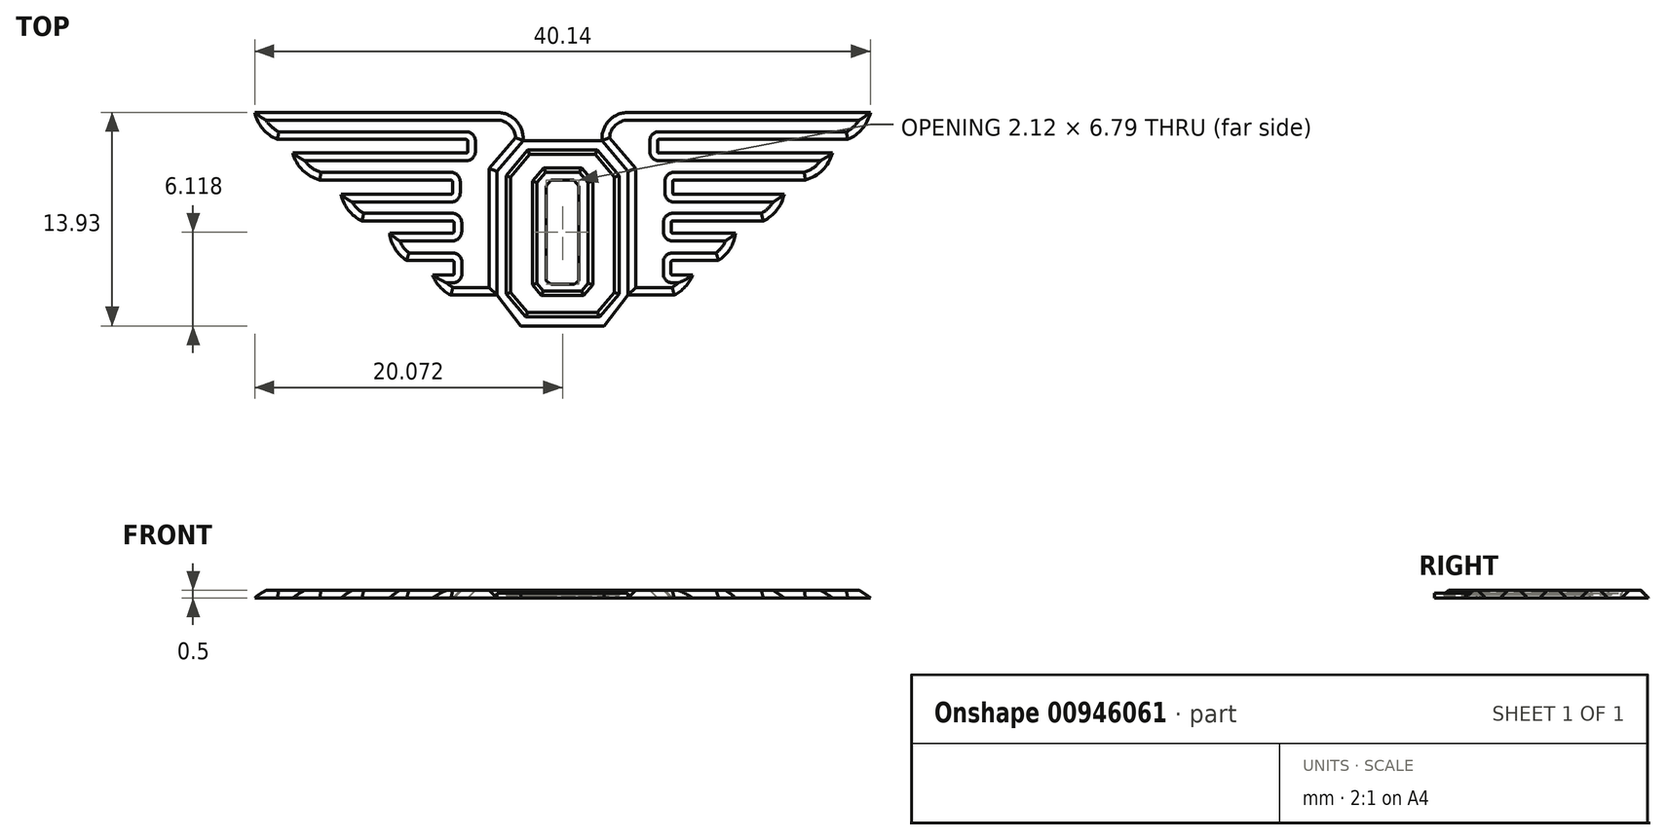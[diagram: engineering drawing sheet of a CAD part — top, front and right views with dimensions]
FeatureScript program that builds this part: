
annotation { "Feature Type Name" : "Feature", "Feature Type Description" : "" }
export const myFeature = defineFeature(function(context is Context, id is Id, definition is map)
    precondition{}
    {
        {
            var Q0;
            Q0=qCreatedBy(makeId("Top.planeOp"),FACE);
            var sketch = newSketch(context, id + "F0", { "sketchPlane" : qUnion([Q0])});
            skLineSegment(sketch, "E0", {"start": v(17.8, 9.2) * mm, "end": v(2, 9.2) * mm});
            skArc(sketch, "E1", {"start": v(2, 9.2) * mm, "mid": v(0.74, 8.65) * mm, "end": v(0.3, 7.37) * mm});
            skLineSegment(sketch, "E2", {"start": v(16.32, 7.44) * mm, "end": v(4, 7.44) * mm});
            skLineSegment(sketch, "E3", {"start": v(3.9, 7.34) * mm, "end": v(3.9, 6.65) * mm});
            skLineSegment(sketch, "E4", {"start": v(4, 6.55) * mm, "end": v(15.3, 6.55) * mm});
            skArc(sketch, "E5", {"start": v(16.32, 7.44) * mm, "mid": v(17.27, 8.14) * mm, "end": v(17.8, 9.2) * mm});
            skLineSegment(sketch, "E6", {"start": v(13.55, 4.8) * mm, "end": v(5, 4.8) * mm});
            skLineSegment(sketch, "E7", {"start": v(4.9, 4.7) * mm, "end": v(4.9, 3.95) * mm});
            skLineSegment(sketch, "E8", {"start": v(5, 3.85) * mm, "end": v(12.16, 3.85) * mm});
            skArc(sketch, "E9", {"start": v(13.55, 4.8) * mm, "mid": v(14.66, 5.44) * mm, "end": v(15.3, 6.55) * mm});
            skLineSegment(sketch, "E10", {"start": v(10.8, 2.12) * mm, "end": v(4.9, 2.12) * mm});
            skLineSegment(sketch, "E11", {"start": v(4.8, 2.02) * mm, "end": v(4.8, 1.42) * mm});
            skLineSegment(sketch, "E12", {"start": v(4.9, 1.32) * mm, "end": v(9, 1.32) * mm});
            skArc(sketch, "E13", {"start": v(10.8, 2.12) * mm, "mid": v(11.68, 2.83) * mm, "end": v(12.16, 3.85) * mm});
            skLineSegment(sketch, "E14", {"start": v(7.89, -0.47) * mm, "end": v(4.89, -0.47) * mm});
            skLineSegment(sketch, "E15", {"start": v(4.79, -0.57) * mm, "end": v(4.79, -1.32) * mm});
            skLineSegment(sketch, "E16", {"start": v(4.89, -1.42) * mm, "end": v(6.2, -1.42) * mm});
            skArc(sketch, "E17", {"start": v(7.89, -0.47) * mm, "mid": v(8.64, 0.3) * mm, "end": v(9, 1.32) * mm});
            skLineSegment(sketch, "E18", {"start": v(5, -2.71) * mm, "end": v(2, -2.71) * mm});
            skLineSegment(sketch, "E19", {"start": v(-2.28, -2) * mm, "end": v(-1.52, -2) * mm});
            skLineSegment(sketch, "E20", {"start": v(-1.52, -2) * mm, "end": v(-1.22, -1.78) * mm});
            skLineSegment(sketch, "E21", {"start": v(-1.22, -1.78) * mm, "end": v(-1.22, 4.4) * mm});
            skLineSegment(sketch, "E22", {"start": v(-1.22, 4.4) * mm, "end": v(-1.53, 4.78) * mm});
            skLineSegment(sketch, "E23", {"start": v(-1.53, 4.78) * mm, "end": v(-2.28, 4.78) * mm});
            skLineSegment(sketch, "E24", {"start": v(-2.28, -5.31) * mm, "end": v(-2.28, 10.14) * mm, "construction": true});
            skArc(sketch, "E25", {"start": v(5, -2.71) * mm, "mid": v(5.71, -2.17) * mm, "end": v(6.2, -1.42) * mm});
            skLineSegment(sketch, "E26", {"start": v(2, -2.71) * mm, "end": v(2, 5.35) * mm});
            skLineSegment(sketch, "E27", {"start": v(2, 5.35) * mm, "end": v(0.3, 7.37) * mm});
            skLineSegment(sketch, "E28", {"start": v(2, -2.71) * mm, "end": v(0.44, -4.73) * mm});
            skLineSegment(sketch, "E29", {"start": v(0.44, -4.73) * mm, "end": v(-2.28, -4.73) * mm});
            skLineSegment(sketch, "E30", {"start": v(0.3, 7.37) * mm, "end": v(-2.28, 7.37) * mm});
            skLineSegment(sketch, "E31", {"start": v(1.4, -2.65) * mm, "end": v(1.4, 4.29) * mm});
            skLineSegment(sketch, "E32", {"start": v(1.4, -2.65) * mm, "end": v(0.13, -4.13) * mm});
            skLineSegment(sketch, "E33", {"start": v(0.13, -4.13) * mm, "end": v(-2.28, -4.13) * mm});
            skLineSegment(sketch, "E34", {"start": v(1.4, 4.29) * mm, "end": v(1.4, 5.08) * mm});
            skLineSegment(sketch, "E35", {"start": v(1.4, 5.08) * mm, "end": v(0, 6.77) * mm});
            skLineSegment(sketch, "E36", {"start": v(0, 6.77) * mm, "end": v(-2.28, 6.77) * mm});
            skLineSegment(sketch, "E37.MirrorCS", {"start": v(-4.85, 7.37) * mm, "end": v(-2.28, 7.37) * mm});
            skLineSegment(sketch, "E38.MirrorCS", {"start": v(-4.56, 6.77) * mm, "end": v(-2.28, 6.77) * mm});
            skLineSegment(sketch, "E39.MirrorCS", {"start": v(-6.55, 5.35) * mm, "end": v(-4.85, 7.37) * mm});
            skLineSegment(sketch, "E40.MirrorCS", {"start": v(-5.95, 5.08) * mm, "end": v(-4.56, 6.77) * mm});
            skLineSegment(sketch, "E41.MirrorCS", {"start": v(-5.95, -2.65) * mm, "end": v(-5.95, 4.29) * mm});
            skLineSegment(sketch, "E42.MirrorCS", {"start": v(-5.95, 4.29) * mm, "end": v(-5.95, 5.08) * mm});
            skLineSegment(sketch, "E43.MirrorCS", {"start": v(-6.55, -2.71) * mm, "end": v(-6.55, 5.35) * mm});
            skLineSegment(sketch, "E44.MirrorCS", {"start": v(-5.95, -2.65) * mm, "end": v(-4.69, -4.13) * mm});
            skLineSegment(sketch, "E45.MirrorCS", {"start": v(-6.55, -2.71) * mm, "end": v(-5, -4.73) * mm});
            skLineSegment(sketch, "E46.MirrorCS", {"start": v(-5, -4.73) * mm, "end": v(-2.28, -4.73) * mm});
            skLineSegment(sketch, "E47.MirrorCS", {"start": v(-4.69, -4.13) * mm, "end": v(-2.28, -4.13) * mm});
            skLineSegment(sketch, "E48.MirrorCS", {"start": v(-2.28, -2) * mm, "end": v(-3.03, -2) * mm});
            skLineSegment(sketch, "E49.MirrorCS", {"start": v(-3.03, -2) * mm, "end": v(-3.34, -1.78) * mm});
            skLineSegment(sketch, "E50.MirrorCS", {"start": v(-3.34, -1.78) * mm, "end": v(-3.34, 4.4) * mm});
            skLineSegment(sketch, "E51.MirrorCS", {"start": v(-3.34, 4.4) * mm, "end": v(-3.02, 4.78) * mm});
            skLineSegment(sketch, "E52.MirrorCS", {"start": v(-3.02, 4.78) * mm, "end": v(-2.28, 4.78) * mm});
            skLineSegment(sketch, "E53.MirrorCS", {"start": v(-9.55, -2.71) * mm, "end": v(-6.55, -2.71) * mm});
            skArc(sketch, "E54.MirrorCS", {"start": v(-9.55, -2.71) * mm, "mid": v(-10.27, -2.17) * mm, "end": v(-10.75, -1.42) * mm});
            skLineSegment(sketch, "E55.MirrorCS", {"start": v(-9.44, -1.42) * mm, "end": v(-10.75, -1.42) * mm});
            skLineSegment(sketch, "E56.MirrorCS", {"start": v(-9.34, -0.57) * mm, "end": v(-9.34, -1.32) * mm});
            skLineSegment(sketch, "E57.MirrorCS", {"start": v(-12.44, -0.47) * mm, "end": v(-9.44, -0.47) * mm});
            skArc(sketch, "E58.MirrorCS", {"start": v(-12.44, -0.47) * mm, "mid": v(-13.2, 0.3) * mm, "end": v(-13.56, 1.32) * mm});
            skLineSegment(sketch, "E59.MirrorCS", {"start": v(-9.46, 1.32) * mm, "end": v(-13.56, 1.32) * mm});
            skLineSegment(sketch, "E60.MirrorCS", {"start": v(-9.36, 2.02) * mm, "end": v(-9.36, 1.42) * mm});
            skLineSegment(sketch, "E61.MirrorCS", {"start": v(-15.36, 2.12) * mm, "end": v(-9.46, 2.12) * mm});
            skArc(sketch, "E62.MirrorCS", {"start": v(-15.36, 2.12) * mm, "mid": v(-16.24, 2.83) * mm, "end": v(-16.72, 3.85) * mm});
            skLineSegment(sketch, "E63.MirrorCS", {"start": v(-9.55, 3.85) * mm, "end": v(-16.72, 3.85) * mm});
            skLineSegment(sketch, "E64.MirrorCS", {"start": v(-9.45, 4.7) * mm, "end": v(-9.45, 3.95) * mm});
            skLineSegment(sketch, "E65.MirrorCS", {"start": v(-18.1, 4.8) * mm, "end": v(-9.55, 4.8) * mm});
            skArc(sketch, "E66.MirrorCS", {"start": v(-18.1, 4.8) * mm, "mid": v(-19.22, 5.44) * mm, "end": v(-19.86, 6.55) * mm});
            skLineSegment(sketch, "E67.MirrorCS", {"start": v(-8.56, 6.55) * mm, "end": v(-19.86, 6.55) * mm});
            skLineSegment(sketch, "E68.MirrorCS", {"start": v(-8.46, 7.34) * mm, "end": v(-8.46, 6.65) * mm});
            skLineSegment(sketch, "E69.MirrorCS", {"start": v(-20.87, 7.44) * mm, "end": v(-8.56, 7.44) * mm});
            skArc(sketch, "E70.MirrorCS", {"start": v(-20.87, 7.44) * mm, "mid": v(-21.82, 8.14) * mm, "end": v(-22.35, 9.2) * mm});
            skLineSegment(sketch, "E71.MirrorCS", {"start": v(-22.35, 9.2) * mm, "end": v(-6.55, 9.2) * mm});
            skArc(sketch, "E72.MirrorCS", {"start": v(-6.55, 9.2) * mm, "mid": v(-5.3, 8.65) * mm, "end": v(-4.85, 7.37) * mm});
            skPoint(sketch, "E73.visualSharp", {"position": v(-9.36, 1.32) * mm});
            skArc(sketch, "E73.filletArc", {"start": v(-9.46, 1.32) * mm, "mid": v(-9.38, 1.35) * mm, "end": v(-9.36, 1.42) * mm});
            skPoint(sketch, "E74.visualSharp", {"position": v(-9.36, 2.12) * mm});
            skArc(sketch, "E74.filletArc", {"start": v(-9.36, 2.02) * mm, "mid": v(-9.38, 2.09) * mm, "end": v(-9.46, 2.12) * mm});
            skPoint(sketch, "E75.visualSharp", {"position": v(-9.34, -0.47) * mm});
            skArc(sketch, "E75.filletArc", {"start": v(-9.34, -0.57) * mm, "mid": v(-9.37, -0.5) * mm, "end": v(-9.44, -0.47) * mm});
            skPoint(sketch, "E76.visualSharp", {"position": v(-9.34, -1.42) * mm});
            skArc(sketch, "E76.filletArc", {"start": v(-9.44, -1.42) * mm, "mid": v(-9.37, -1.39) * mm, "end": v(-9.34, -1.32) * mm});
            skPoint(sketch, "E77.visualSharp", {"position": v(-9.45, 3.85) * mm});
            skArc(sketch, "E77.filletArc", {"start": v(-9.55, 3.85) * mm, "mid": v(-9.48, 3.88) * mm, "end": v(-9.45, 3.95) * mm});
            skPoint(sketch, "E78.visualSharp", {"position": v(-9.45, 4.8) * mm});
            skArc(sketch, "E78.filletArc", {"start": v(-9.45, 4.7) * mm, "mid": v(-9.48, 4.76) * mm, "end": v(-9.55, 4.8) * mm});
            skPoint(sketch, "E79.visualSharp", {"position": v(-8.46, 6.55) * mm});
            skArc(sketch, "E79.filletArc", {"start": v(-8.56, 6.55) * mm, "mid": v(-8.5, 6.58) * mm, "end": v(-8.46, 6.65) * mm});
            skPoint(sketch, "E80.visualSharp", {"position": v(-8.46, 7.44) * mm});
            skArc(sketch, "E80.filletArc", {"start": v(-8.46, 7.34) * mm, "mid": v(-8.5, 7.41) * mm, "end": v(-8.56, 7.44) * mm});
            skPoint(sketch, "E81.visualSharp", {"position": v(3.9, 7.44) * mm});
            skArc(sketch, "E81.filletArc", {"start": v(4, 7.44) * mm, "mid": v(3.94, 7.41) * mm, "end": v(3.9, 7.34) * mm});
            skPoint(sketch, "E82.visualSharp", {"position": v(3.9, 6.55) * mm});
            skArc(sketch, "E82.filletArc", {"start": v(3.9, 6.65) * mm, "mid": v(3.94, 6.58) * mm, "end": v(4, 6.55) * mm});
            skPoint(sketch, "E83.visualSharp", {"position": v(4.9, 4.8) * mm});
            skArc(sketch, "E83.filletArc", {"start": v(5, 4.8) * mm, "mid": v(4.93, 4.76) * mm, "end": v(4.9, 4.7) * mm});
            skPoint(sketch, "E84.visualSharp", {"position": v(4.9, 3.85) * mm});
            skArc(sketch, "E84.filletArc", {"start": v(4.9, 3.95) * mm, "mid": v(4.93, 3.88) * mm, "end": v(5, 3.85) * mm});
            skPoint(sketch, "E85.visualSharp", {"position": v(4.8, 2.12) * mm});
            skArc(sketch, "E85.filletArc", {"start": v(4.9, 2.12) * mm, "mid": v(4.83, 2.09) * mm, "end": v(4.8, 2.02) * mm});
            skPoint(sketch, "E86.visualSharp", {"position": v(4.8, 1.32) * mm});
            skArc(sketch, "E86.filletArc", {"start": v(4.8, 1.42) * mm, "mid": v(4.83, 1.35) * mm, "end": v(4.9, 1.32) * mm});
            skPoint(sketch, "E87.visualSharp", {"position": v(4.79, -0.47) * mm});
            skArc(sketch, "E87.filletArc", {"start": v(4.89, -0.47) * mm, "mid": v(4.82, -0.5) * mm, "end": v(4.79, -0.57) * mm});
            skPoint(sketch, "E88.visualSharp", {"position": v(4.79, -1.42) * mm});
            skArc(sketch, "E88.filletArc", {"start": v(4.79, -1.32) * mm, "mid": v(4.82, -1.39) * mm, "end": v(4.89, -1.42) * mm});
            skLineSegment(sketch, "E89", {"start": v(-2.28, 5.29) * mm, "end": v(-1.18, 5.29) * mm});
            skLineSegment(sketch, "E90", {"start": v(-1.18, 5.29) * mm, "end": v(-0.6, 4.62) * mm});
            skLineSegment(sketch, "E91", {"start": v(-0.6, 4.62) * mm, "end": v(-0.6, -1.94) * mm});
            skLineSegment(sketch, "E92", {"start": v(-0.6, -1.94) * mm, "end": v(-1.03, -2.44) * mm});
            skLineSegment(sketch, "E93", {"start": v(-1.03, -2.44) * mm, "end": v(-2.28, -2.44) * mm});
            skLineSegment(sketch, "E94.MirrorCS", {"start": v(-2.28, 5.29) * mm, "end": v(-3.38, 5.29) * mm});
            skLineSegment(sketch, "E95.MirrorCS", {"start": v(-3.38, 5.29) * mm, "end": v(-3.95, 4.62) * mm});
            skLineSegment(sketch, "E96.MirrorCS", {"start": v(-3.95, 4.62) * mm, "end": v(-3.95, -1.94) * mm});
            skLineSegment(sketch, "E97.MirrorCS", {"start": v(-3.95, -1.94) * mm, "end": v(-3.53, -2.44) * mm});
            skLineSegment(sketch, "E98.MirrorCS", {"start": v(-3.53, -2.44) * mm, "end": v(-2.28, -2.44) * mm});
            skLineSegment(sketch, "E99", {"start": v(2, -2.91) * mm, "end": v(0.3, 7.37) * mm, "construction": true});
            skSolve(sketch);
        }
        {
            var Q0;
            Q0=makeQuery(id+"F0.imprint","IMPRINT",FACE,{"disambiguationData":[TD([[makeQuery(id+"F0.imprint","IMPRINT",EDGE,{"derivedFrom":sQuery(id+"F0.wireOp",EDGE,"E31")}),1.0]])]});
            var Q1;
            Q1=makeQuery(id+"F0.imprint","IMPRINT",FACE,{"disambiguationData":[TD([[makeQuery(id+"F0.imprint","IMPRINT",EDGE,{"derivedFrom":sQuery(id+"F0.wireOp",EDGE,"E0")}),1.0]])]});
            var Q2;
            Q2=makeQuery(id+"F0.imprint","IMPRINT",FACE,{"disambiguationData":[TD([[makeQuery(id+"F0.imprint","IMPRINT",EDGE,{"derivedFrom":sQuery(id+"F0.wireOp",EDGE,"E39.MirrorCS")}),1.0]])]});
            extrude(context, id + "F1", {"entities" : qUnion([Q0, Q1, Q2]), "depth" : 0.5 * mm, "offsetDistance" : 25 * mm});
        }
        {
            var Q0;
            Q0=makeQuery(id+"F0.imprint","IMPRINT",FACE,{"disambiguationData":[TD([[makeQuery(id+"F0.imprint","IMPRINT",EDGE,{"derivedFrom":sQuery(id+"F0.wireOp",EDGE,"E26")}),1.0]])]});
            var Q1;
            Q1=makeQuery(id+"F0.imprint","IMPRINT",FACE,{"disambiguationData":[TD([[makeQuery(id+"F0.imprint","IMPRINT",EDGE,{"derivedFrom":sQuery(id+"F0.wireOp",EDGE,"E19")}),-1.0]])]});
            extrude(context, id + "F2", {"entities" : qUnion([Q0, Q1]), "depth" : 0.3 * mm, "offsetDistance" : 25 * mm});
        }
        {
            var Q0;
            Q0=makeQuery(id+"F1.opExtrude","CAP_FACE",FACE,{"disambiguationData":[OSD([sQuery(id+"F0.wireOp",EDGE,"E39.MirrorCS"),sQuery(id+"F0.wireOp",EDGE,"E43.MirrorCS"),sQuery(id+"F0.wireOp",EDGE,"E53.MirrorCS"),sQuery(id+"F0.wireOp",EDGE,"E54.MirrorCS"),sQuery(id+"F0.wireOp",EDGE,"E55.MirrorCS"),sQuery(id+"F0.wireOp",EDGE,"E56.MirrorCS"),sQuery(id+"F0.wireOp",EDGE,"E57.MirrorCS"),sQuery(id+"F0.wireOp",EDGE,"E58.MirrorCS"),sQuery(id+"F0.wireOp",EDGE,"E59.MirrorCS"),sQuery(id+"F0.wireOp",EDGE,"E60.MirrorCS"),sQuery(id+"F0.wireOp",EDGE,"E61.MirrorCS"),sQuery(id+"F0.wireOp",EDGE,"E62.MirrorCS"),sQuery(id+"F0.wireOp",EDGE,"E63.MirrorCS"),sQuery(id+"F0.wireOp",EDGE,"E64.MirrorCS"),sQuery(id+"F0.wireOp",EDGE,"E65.MirrorCS"),sQuery(id+"F0.wireOp",EDGE,"E66.MirrorCS"),sQuery(id+"F0.wireOp",EDGE,"E67.MirrorCS"),sQuery(id+"F0.wireOp",EDGE,"E68.MirrorCS"),sQuery(id+"F0.wireOp",EDGE,"E69.MirrorCS"),sQuery(id+"F0.wireOp",EDGE,"E70.MirrorCS"),sQuery(id+"F0.wireOp",EDGE,"E71.MirrorCS"),sQuery(id+"F0.wireOp",EDGE,"E72.MirrorCS"),sQuery(id+"F0.wireOp",EDGE,"E73.filletArc"),sQuery(id+"F0.wireOp",EDGE,"E74.filletArc"),sQuery(id+"F0.wireOp",EDGE,"E75.filletArc"),sQuery(id+"F0.wireOp",EDGE,"E76.filletArc"),sQuery(id+"F0.wireOp",EDGE,"E77.filletArc"),sQuery(id+"F0.wireOp",EDGE,"E78.filletArc"),sQuery(id+"F0.wireOp",EDGE,"E79.filletArc"),sQuery(id+"F0.wireOp",EDGE,"E80.filletArc")])],"isStart":false});
            var Q1;
            Q1=makeQuery(id+"F1.opExtrude","CAP_FACE",FACE,{"disambiguationData":[OSD([sQuery(id+"F0.wireOp",EDGE,"E0"),sQuery(id+"F0.wireOp",EDGE,"E1"),sQuery(id+"F0.wireOp",EDGE,"E2"),sQuery(id+"F0.wireOp",EDGE,"E3"),sQuery(id+"F0.wireOp",EDGE,"E4"),sQuery(id+"F0.wireOp",EDGE,"E5"),sQuery(id+"F0.wireOp",EDGE,"E6"),sQuery(id+"F0.wireOp",EDGE,"E7"),sQuery(id+"F0.wireOp",EDGE,"E8"),sQuery(id+"F0.wireOp",EDGE,"E9"),sQuery(id+"F0.wireOp",EDGE,"E10"),sQuery(id+"F0.wireOp",EDGE,"E11"),sQuery(id+"F0.wireOp",EDGE,"E12"),sQuery(id+"F0.wireOp",EDGE,"E13"),sQuery(id+"F0.wireOp",EDGE,"E14"),sQuery(id+"F0.wireOp",EDGE,"E15"),sQuery(id+"F0.wireOp",EDGE,"E16"),sQuery(id+"F0.wireOp",EDGE,"E17"),sQuery(id+"F0.wireOp",EDGE,"E18"),sQuery(id+"F0.wireOp",EDGE,"E25"),sQuery(id+"F0.wireOp",EDGE,"E26"),sQuery(id+"F0.wireOp",EDGE,"E27"),sQuery(id+"F0.wireOp",EDGE,"E81.filletArc"),sQuery(id+"F0.wireOp",EDGE,"E82.filletArc"),sQuery(id+"F0.wireOp",EDGE,"E83.filletArc"),sQuery(id+"F0.wireOp",EDGE,"E84.filletArc"),sQuery(id+"F0.wireOp",EDGE,"E85.filletArc"),sQuery(id+"F0.wireOp",EDGE,"E86.filletArc"),sQuery(id+"F0.wireOp",EDGE,"E87.filletArc"),sQuery(id+"F0.wireOp",EDGE,"E88.filletArc")])],"isStart":false});
            chamfer(context, id + "F3", {"entities" : qUnion([Q0, Q1]), "width" : 0.5 * mm, "tangentPropagation" : true});
        }
        {
            var Q0;
            Q0=makeQuery(id+"F1.opExtrude","CAP_FACE",FACE,{"disambiguationData":[OSD([sQuery(id+"F0.wireOp",EDGE,"E31"),sQuery(id+"F0.wireOp",EDGE,"E32"),sQuery(id+"F0.wireOp",EDGE,"E33"),sQuery(id+"F0.wireOp",EDGE,"E34"),sQuery(id+"F0.wireOp",EDGE,"E35"),sQuery(id+"F0.wireOp",EDGE,"E36"),sQuery(id+"F0.wireOp",EDGE,"E38.MirrorCS"),sQuery(id+"F0.wireOp",EDGE,"E40.MirrorCS"),sQuery(id+"F0.wireOp",EDGE,"E41.MirrorCS"),sQuery(id+"F0.wireOp",EDGE,"E42.MirrorCS"),sQuery(id+"F0.wireOp",EDGE,"E44.MirrorCS"),sQuery(id+"F0.wireOp",EDGE,"E47.MirrorCS"),sQuery(id+"F0.wireOp",EDGE,"E89"),sQuery(id+"F0.wireOp",EDGE,"E90"),sQuery(id+"F0.wireOp",EDGE,"E91"),sQuery(id+"F0.wireOp",EDGE,"E92"),sQuery(id+"F0.wireOp",EDGE,"E93"),sQuery(id+"F0.wireOp",EDGE,"E94.MirrorCS"),sQuery(id+"F0.wireOp",EDGE,"E95.MirrorCS"),sQuery(id+"F0.wireOp",EDGE,"E96.MirrorCS"),sQuery(id+"F0.wireOp",EDGE,"E97.MirrorCS"),sQuery(id+"F0.wireOp",EDGE,"E98.MirrorCS")])],"isStart":false});
            chamfer(context, id + "F4", {"entities" : qUnion([Q0]), "width" : 0.3 * mm, "tangentPropagation" : true});
        }
        {
            var Q0;
            Q0=makeQuery(id+"F2.opExtrude","SWEPT_BODY",BODY,{"disambiguationData":[OSD([sQuery(id+"F0.wireOp",EDGE,"E26"),sQuery(id+"F0.wireOp",EDGE,"E27"),sQuery(id+"F0.wireOp",EDGE,"E28"),sQuery(id+"F0.wireOp",EDGE,"E29"),sQuery(id+"F0.wireOp",EDGE,"E30"),sQuery(id+"F0.wireOp",EDGE,"E31"),sQuery(id+"F0.wireOp",EDGE,"E32"),sQuery(id+"F0.wireOp",EDGE,"E33"),sQuery(id+"F0.wireOp",EDGE,"E34"),sQuery(id+"F0.wireOp",EDGE,"E35"),sQuery(id+"F0.wireOp",EDGE,"E36"),sQuery(id+"F0.wireOp",EDGE,"E37.MirrorCS"),sQuery(id+"F0.wireOp",EDGE,"E38.MirrorCS"),sQuery(id+"F0.wireOp",EDGE,"E39.MirrorCS"),sQuery(id+"F0.wireOp",EDGE,"E40.MirrorCS"),sQuery(id+"F0.wireOp",EDGE,"E41.MirrorCS"),sQuery(id+"F0.wireOp",EDGE,"E42.MirrorCS"),sQuery(id+"F0.wireOp",EDGE,"E43.MirrorCS"),sQuery(id+"F0.wireOp",EDGE,"E44.MirrorCS"),sQuery(id+"F0.wireOp",EDGE,"E45.MirrorCS"),sQuery(id+"F0.wireOp",EDGE,"E46.MirrorCS"),sQuery(id+"F0.wireOp",EDGE,"E47.MirrorCS")])]});
            var Q1;
            Q1=makeQuery(id+"F1.opExtrude","SWEPT_BODY",BODY,{"disambiguationData":[OSD([sQuery(id+"F0.wireOp",EDGE,"E39.MirrorCS"),sQuery(id+"F0.wireOp",EDGE,"E43.MirrorCS"),sQuery(id+"F0.wireOp",EDGE,"E53.MirrorCS"),sQuery(id+"F0.wireOp",EDGE,"E54.MirrorCS"),sQuery(id+"F0.wireOp",EDGE,"E55.MirrorCS"),sQuery(id+"F0.wireOp",EDGE,"E56.MirrorCS"),sQuery(id+"F0.wireOp",EDGE,"E57.MirrorCS"),sQuery(id+"F0.wireOp",EDGE,"E58.MirrorCS"),sQuery(id+"F0.wireOp",EDGE,"E59.MirrorCS"),sQuery(id+"F0.wireOp",EDGE,"E60.MirrorCS"),sQuery(id+"F0.wireOp",EDGE,"E61.MirrorCS"),sQuery(id+"F0.wireOp",EDGE,"E62.MirrorCS"),sQuery(id+"F0.wireOp",EDGE,"E63.MirrorCS"),sQuery(id+"F0.wireOp",EDGE,"E64.MirrorCS"),sQuery(id+"F0.wireOp",EDGE,"E65.MirrorCS"),sQuery(id+"F0.wireOp",EDGE,"E66.MirrorCS"),sQuery(id+"F0.wireOp",EDGE,"E67.MirrorCS"),sQuery(id+"F0.wireOp",EDGE,"E68.MirrorCS"),sQuery(id+"F0.wireOp",EDGE,"E69.MirrorCS"),sQuery(id+"F0.wireOp",EDGE,"E70.MirrorCS"),sQuery(id+"F0.wireOp",EDGE,"E71.MirrorCS"),sQuery(id+"F0.wireOp",EDGE,"E72.MirrorCS"),sQuery(id+"F0.wireOp",EDGE,"E73.filletArc"),sQuery(id+"F0.wireOp",EDGE,"E74.filletArc"),sQuery(id+"F0.wireOp",EDGE,"E75.filletArc"),sQuery(id+"F0.wireOp",EDGE,"E76.filletArc"),sQuery(id+"F0.wireOp",EDGE,"E77.filletArc"),sQuery(id+"F0.wireOp",EDGE,"E78.filletArc"),sQuery(id+"F0.wireOp",EDGE,"E79.filletArc"),sQuery(id+"F0.wireOp",EDGE,"E80.filletArc")])]});
            var Q2;
            Q2=makeQuery(id+"F1.opExtrude","SWEPT_BODY",BODY,{"disambiguationData":[OSD([sQuery(id+"F0.wireOp",EDGE,"E31"),sQuery(id+"F0.wireOp",EDGE,"E32"),sQuery(id+"F0.wireOp",EDGE,"E33"),sQuery(id+"F0.wireOp",EDGE,"E34"),sQuery(id+"F0.wireOp",EDGE,"E35"),sQuery(id+"F0.wireOp",EDGE,"E36"),sQuery(id+"F0.wireOp",EDGE,"E38.MirrorCS"),sQuery(id+"F0.wireOp",EDGE,"E40.MirrorCS"),sQuery(id+"F0.wireOp",EDGE,"E41.MirrorCS"),sQuery(id+"F0.wireOp",EDGE,"E42.MirrorCS"),sQuery(id+"F0.wireOp",EDGE,"E44.MirrorCS"),sQuery(id+"F0.wireOp",EDGE,"E47.MirrorCS"),sQuery(id+"F0.wireOp",EDGE,"E89"),sQuery(id+"F0.wireOp",EDGE,"E90"),sQuery(id+"F0.wireOp",EDGE,"E91"),sQuery(id+"F0.wireOp",EDGE,"E92"),sQuery(id+"F0.wireOp",EDGE,"E93"),sQuery(id+"F0.wireOp",EDGE,"E94.MirrorCS"),sQuery(id+"F0.wireOp",EDGE,"E95.MirrorCS"),sQuery(id+"F0.wireOp",EDGE,"E96.MirrorCS"),sQuery(id+"F0.wireOp",EDGE,"E97.MirrorCS"),sQuery(id+"F0.wireOp",EDGE,"E98.MirrorCS")])]});
            var Q3;
            Q3=makeQuery(id+"F2.opExtrude","SWEPT_BODY",BODY,{"disambiguationData":[OSD([sQuery(id+"F0.wireOp",EDGE,"E19"),sQuery(id+"F0.wireOp",EDGE,"E20"),sQuery(id+"F0.wireOp",EDGE,"E21"),sQuery(id+"F0.wireOp",EDGE,"E22"),sQuery(id+"F0.wireOp",EDGE,"E23"),sQuery(id+"F0.wireOp",EDGE,"E48.MirrorCS"),sQuery(id+"F0.wireOp",EDGE,"E49.MirrorCS"),sQuery(id+"F0.wireOp",EDGE,"E50.MirrorCS"),sQuery(id+"F0.wireOp",EDGE,"E51.MirrorCS"),sQuery(id+"F0.wireOp",EDGE,"E52.MirrorCS"),sQuery(id+"F0.wireOp",EDGE,"E89"),sQuery(id+"F0.wireOp",EDGE,"E90"),sQuery(id+"F0.wireOp",EDGE,"E91"),sQuery(id+"F0.wireOp",EDGE,"E92"),sQuery(id+"F0.wireOp",EDGE,"E93"),sQuery(id+"F0.wireOp",EDGE,"E94.MirrorCS"),sQuery(id+"F0.wireOp",EDGE,"E95.MirrorCS"),sQuery(id+"F0.wireOp",EDGE,"E96.MirrorCS"),sQuery(id+"F0.wireOp",EDGE,"E97.MirrorCS"),sQuery(id+"F0.wireOp",EDGE,"E98.MirrorCS")])]});
            var Q4;
            Q4=makeQuery(id+"F1.opExtrude","SWEPT_BODY",BODY,{"disambiguationData":[OSD([sQuery(id+"F0.wireOp",EDGE,"E0"),sQuery(id+"F0.wireOp",EDGE,"E1"),sQuery(id+"F0.wireOp",EDGE,"E2"),sQuery(id+"F0.wireOp",EDGE,"E3"),sQuery(id+"F0.wireOp",EDGE,"E4"),sQuery(id+"F0.wireOp",EDGE,"E5"),sQuery(id+"F0.wireOp",EDGE,"E6"),sQuery(id+"F0.wireOp",EDGE,"E7"),sQuery(id+"F0.wireOp",EDGE,"E8"),sQuery(id+"F0.wireOp",EDGE,"E9"),sQuery(id+"F0.wireOp",EDGE,"E10"),sQuery(id+"F0.wireOp",EDGE,"E11"),sQuery(id+"F0.wireOp",EDGE,"E12"),sQuery(id+"F0.wireOp",EDGE,"E13"),sQuery(id+"F0.wireOp",EDGE,"E14"),sQuery(id+"F0.wireOp",EDGE,"E15"),sQuery(id+"F0.wireOp",EDGE,"E16"),sQuery(id+"F0.wireOp",EDGE,"E17"),sQuery(id+"F0.wireOp",EDGE,"E18"),sQuery(id+"F0.wireOp",EDGE,"E25"),sQuery(id+"F0.wireOp",EDGE,"E26"),sQuery(id+"F0.wireOp",EDGE,"E27"),sQuery(id+"F0.wireOp",EDGE,"E81.filletArc"),sQuery(id+"F0.wireOp",EDGE,"E82.filletArc"),sQuery(id+"F0.wireOp",EDGE,"E83.filletArc"),sQuery(id+"F0.wireOp",EDGE,"E84.filletArc"),sQuery(id+"F0.wireOp",EDGE,"E85.filletArc"),sQuery(id+"F0.wireOp",EDGE,"E86.filletArc"),sQuery(id+"F0.wireOp",EDGE,"E87.filletArc"),sQuery(id+"F0.wireOp",EDGE,"E88.filletArc")])]});
            booleanBodies(context, id + "F5", {"operationType" : BooleanOperationType.UNION, "tools" : qUnion([Q0, Q1, Q2, Q3, Q4])});
        }
    });
